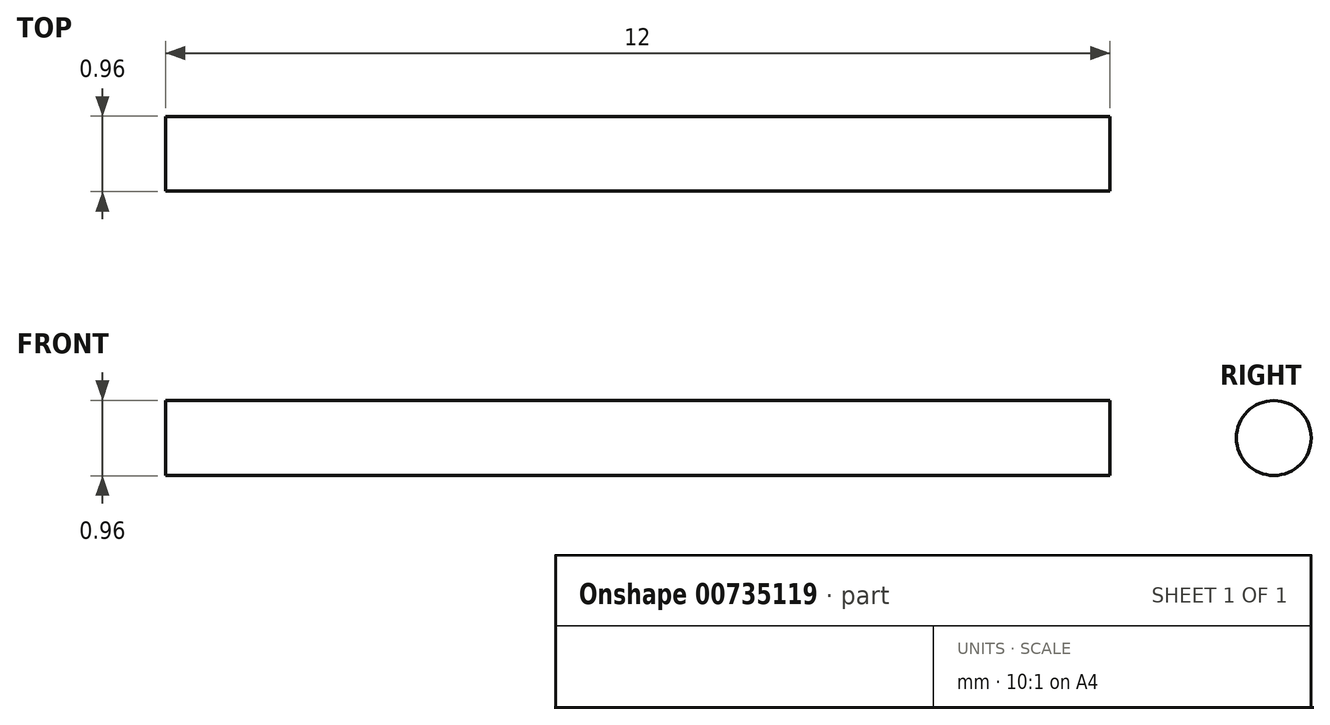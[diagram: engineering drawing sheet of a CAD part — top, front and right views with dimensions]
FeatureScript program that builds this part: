
annotation { "Feature Type Name" : "Feature", "Feature Type Description" : "" }
export const myFeature = defineFeature(function(context is Context, id is Id, definition is map)
    precondition{}
    {
        {
            var Q0;
            Q0=qCreatedBy(makeId("Right.planeOp"),FACE);
            var sketch = newSketch(context, id + "F0", { "sketchPlane" : qUnion([Q0])});
            skCircle(sketch, "E0", {"center": v(0, 0) * mm, "radius": 0.48 * mm});
            skSolve(sketch);
        }
        {
            var Q0;
            Q0 = qSketchRegion(id + "F0", true);
            extrude(context, id + "F1", {"entities" : qUnion([Q0]), "oppositeDirection" : true, "depth" : 12 * mm, "offsetDistance" : 25 * mm});
        }
    });
